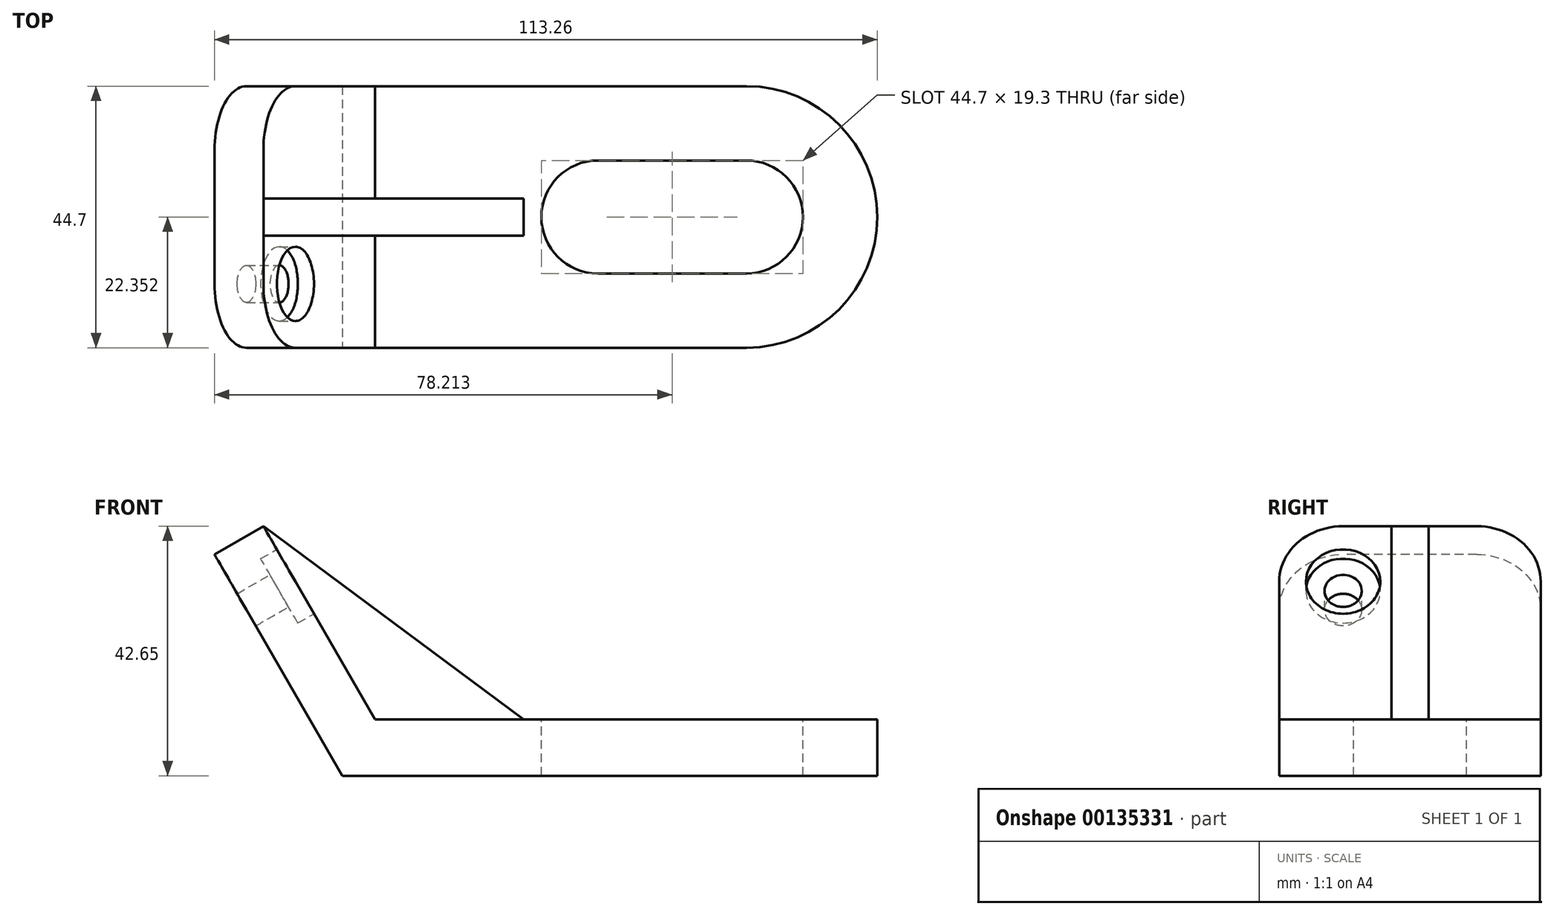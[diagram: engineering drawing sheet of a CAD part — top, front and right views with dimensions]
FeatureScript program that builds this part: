
annotation { "Feature Type Name" : "Feature", "Feature Type Description" : "" }
export const myFeature = defineFeature(function(context is Context, id is Id, definition is map)
    precondition{}
    {
        {
            var Q0;
            Q0=qCreatedBy(makeId("Front.planeOp"),FACE);
            var sketch = newSketch(context, id + "F0", { "sketchPlane" : qUnion([Q0])});
            skLineSegment(sketch, "E0", {"start": v(0, 0) * mm, "end": v(69.07, 0) * mm});
            skLineSegment(sketch, "E1", {"start": v(69.07, 0) * mm, "end": v(69.07, 9.65) * mm});
            skLineSegment(sketch, "E2", {"start": v(69.07, 9.65) * mm, "end": v(5.57, 9.65) * mm});
            skLineSegment(sketch, "E3", {"start": v(5.57, 9.65) * mm, "end": v(-13.48, 42.65) * mm});
            skLineSegment(sketch, "E4", {"start": v(-13.48, 42.65) * mm, "end": v(-21.84, 37.82) * mm});
            skLineSegment(sketch, "E5", {"start": v(-21.84, 37.82) * mm, "end": v(0, 0) * mm});
            skSolve(sketch);
        }
        {
            var Q0;
            Q0 = qSketchRegion(id + "F0", true);
            extrude(context, id + "F1", {"entities" : qUnion([Q0]), "oppositeDirection" : true, "depth" : 44.7 * mm});
        }
        {
            var Q0;
            Q0=makeQuery(id+"F1.opExtrude","SWEPT_FACE",FACE,{"disambiguationData":[OSD([sQuery(id+"F0.wireOp",EDGE,"E2")])]});
            var sketch = newSketch(context, id + "F2", { "sketchPlane" : qUnion([Q0])});
            skArc(sketch, "E6", {"start": v(69.07, 0) * mm, "mid": v(91.42, 22.35) * mm, "end": v(69.07, 44.7) * mm});
            skArc(sketch, "E7", {"start": v(69.07, 12.7) * mm, "mid": v(78.72, 22.35) * mm, "end": v(69.07, 32) * mm});
            skLineSegment(sketch, "E8", {"start": v(69.07, 22.35) * mm, "end": v(43.67, 22.35) * mm, "construction": true});
            skArc(sketch, "E9", {"start": v(43.67, 32) * mm, "mid": v(34.02, 22.35) * mm, "end": v(43.67, 12.7) * mm});
            skLineSegment(sketch, "E10", {"start": v(43.67, 32) * mm, "end": v(69.07, 32) * mm});
            skLineSegment(sketch, "E11", {"start": v(43.67, 12.7) * mm, "end": v(69.07, 12.7) * mm});
            skLineSegment(sketch, "E12.trimOffspring", {"start": v(69.07, 12.7) * mm, "end": v(69.07, 0) * mm});
            skLineSegment(sketch, "E13", {"start": v(5.57, 22.35) * mm, "end": v(30.97, 22.35) * mm, "construction": true});
            skPoint(sketch, "E13.endSnap0", {"position": v(34.02, 22.35) * mm});
            skSolve(sketch);
        }
        {
            var Q0;
            {var subQ0=sQuery(id+"F2.wireOp",EDGE,"E6");Q0=makeQuery(id+"F2.imprint","IMPRINT",FACE,{"disambiguationData":[TD([[makeQuery(id+"F2.imprint","IMPRINT",EDGE,{"derivedFrom":subQ0}),1.0]])]});}
            var Q1;
            Q1=makeQuery(id+"F1.opExtrude","SWEPT_FACE",FACE,{"disambiguationData":[OSD([sQuery(id+"F0.wireOp",EDGE,"E0")])]});
            extrude(context, id + "F3", {"entities" : qUnion([Q0]), "operationType" : NewBodyOperationType.ADD, "endBound" : BoundingType.UP_TO_SURFACE, "oppositeDirection" : true, "endBoundEntityFace" : qUnion([Q1]), "depth" : 25.4 * mm});
        }
        {
            var Q0;
            Q0=makeQuery(id+"F2.imprint","IMPRINT",FACE,{"disambiguationData":[TD([[makeQuery(id+"F2.imprint","IMPRINT",EDGE,{"derivedFrom":sQuery(id+"F2.wireOp",EDGE,"E9")}),1.0]])]});
            var Q1;
            {var subQ0=sQuery(id+"F0.wireOp",EDGE,"E0");Q1=makeQuery(id+"F3.boolean.opBoolean","MERGE",FACE,{"derivedFrom":[makeQuery(id+"F1.opExtrude","SWEPT_FACE",FACE,{"disambiguationData":[OSD([subQ0])]}),makeQuery(id+"F3.opExtrude","CAP_FACE",FACE,{"disambiguationData":[OSD([subQ0])],"isStart":false})]});}
            extrude(context, id + "F4", {"entities" : qUnion([Q0]), "operationType" : NewBodyOperationType.REMOVE, "endBound" : BoundingType.UP_TO_SURFACE, "oppositeDirection" : true, "endBoundEntityFace" : qUnion([Q1]), "depth" : 25.4 * mm});
        }
        {
            var Q0;
            Q0=qCreatedBy(makeId("Front.planeOp"),FACE);
            cPlane(context, id + "F5", {"entities" : qUnion([Q0]), "cplaneType" : CPlaneType.OFFSET, "offset" : 22.35 * mm, "oppositeDirection" : true, "width" : 152.4 * mm, "height" : 152.4 * mm});
        }
        {
            var Q0;
            Q0=makeQuery(id+"F1.opExtrude","SWEPT_FACE",FACE,{"disambiguationData":[OSD([sQuery(id+"F0.wireOp",EDGE,"E3")])]});
            var sketch = newSketch(context, id + "F6", { "sketchPlane" : qUnion([Q0])});
            skPoint(sketch, "E14", {"position": v(22.35, 43.67) * mm});
            skSolve(sketch);
        }
        {
            var Q0;
            Q0=qCreatedBy(id+"F5.planeOp",FACE);
            var sketch = newSketch(context, id + "F7", { "sketchPlane" : qUnion([Q0])});
            skPoint(sketch, "E15.0", {"position": v(30.97, 9.65) * mm});
            skPoint(sketch, "E16.0", {"position": v(-13.48, 42.65) * mm});
            skLineSegment(sketch, "E17", {"start": v(-13.48, 42.65) * mm, "end": v(30.97, 9.65) * mm});
            skPoint(sketch, "E18.0", {"position": v(5.57, 9.65) * mm});
            skLineSegment(sketch, "E19", {"start": v(30.97, 9.65) * mm, "end": v(5.57, 9.65) * mm});
            skLineSegment(sketch, "E20", {"start": v(-13.48, 42.65) * mm, "end": v(5.57, 9.65) * mm});
            skSolve(sketch);
        }
        {
            var Q0;
            Q0=makeQuery(id+"F7.imprint","IMPRINT",FACE,{"disambiguationData":[TD([[makeQuery(id+"F7.imprint","IMPRINT",EDGE,{"derivedFrom":sQuery(id+"F7.wireOp",EDGE,"E17")}),-1.0]])]});
            extrude(context, id + "F8", {"entities" : qUnion([Q0]), "operationType" : NewBodyOperationType.ADD, "endBound" : BoundingType.SYMMETRIC, "depth" : 6.35 * mm});
        }
        {
            var Q0;
            {var subQ0=sQuery(id+"F0.wireOp",EDGE,"E3");Q0=makeQuery(id+"F6.imprint","IMPRINT",FACE,{"disambiguationData":[TD([[makeQuery(id+"F6.imprint","IMPRINT",EDGE,{"derivedFrom":makeQuery(id+"F1.opExtrude","CAP_EDGE",EDGE,{"disambiguationData":[OSD([subQ0])],"isStart":true})}),-1.0]])]});}
            var sketch = newSketch(context, id + "F9", { "sketchPlane" : qUnion([Q0])});
            skLineSegment(sketch, "E21.0.0", {"start": v(0, 43.67) * mm, "end": v(0, 5.57) * mm});
            skLineSegment(sketch, "E21.0.1", {"start": v(0, 5.57) * mm, "end": v(44.7, 5.57) * mm});
            skLineSegment(sketch, "E21.0.2", {"start": v(44.7, 5.57) * mm, "end": v(44.7, 43.67) * mm});
            skLineSegment(sketch, "E21.0.3", {"start": v(44.7, 43.67) * mm, "end": v(0, 43.67) * mm});
            skLineSegment(sketch, "E22", {"start": v(44.7, 32.75) * mm, "end": v(33.78, 32.75) * mm});
            skLineSegment(sketch, "E23", {"start": v(44.7, 32.75) * mm, "end": v(10.92, 32.75) * mm});
            skPoint(sketch, "E24.0", {"position": v(22.35, 43.67) * mm});
            skCircle(sketch, "E25", {"center": v(33.78, 32.75) * mm, "radius": 6.35 * mm});
            skCircle(sketch, "E26", {"center": v(10.92, 32.75) * mm, "radius": 6.35 * mm});
            skCircle(sketch, "E27", {"center": v(10.92, 32.75) * mm, "radius": 3.18 * mm});
            skCircle(sketch, "E28", {"center": v(33.78, 32.75) * mm, "radius": 3.18 * mm});
            skSolve(sketch);
        }
        {
            var Q0;
            {var subQ0=sQuery(id+"F9.wireOp",EDGE,"E23");var subQ1=makeQuery(id+"F9.imprint","IMPRINT",VERTEX,{"derivedFrom":subQ0});Q0=makeQuery(id+"F9.imprint","IMPRINT",FACE,{"disambiguationData":[TD([[makeQuery(id+"F9.imprint","IMPRINT",EDGE,{"disambiguationData":[TD([[subQ1,1.0]])],"derivedFrom":subQ0}),-1.0]])]});}
            var Q1;
            {var subQ0=sQuery(id+"F9.wireOp",EDGE,"E23");var subQ1=makeQuery(id+"F9.imprint","IMPRINT",VERTEX,{"derivedFrom":subQ0});Q1=makeQuery(id+"F9.imprint","IMPRINT",FACE,{"disambiguationData":[TD([[makeQuery(id+"F9.imprint","IMPRINT",EDGE,{"disambiguationData":[TD([[subQ1,1.0]])],"derivedFrom":subQ0}),1.0]])]});}
            var Q2;
            Q2=makeQuery(id+"F9.imprint","IMPRINT",FACE,{"disambiguationData":[TD([[makeQuery(id+"F9.imprint","IMPRINT",EDGE,{"derivedFrom":sQuery(id+"F9.wireOp",EDGE,"E27")}),1.0]])]});
            var Q3;
            Q3=makeQuery(id+"F1.opExtrude","SWEPT_FACE",FACE,{"disambiguationData":[OSD([sQuery(id+"F0.wireOp",EDGE,"E5")])]});
            extrude(context, id + "F10", {"entities" : qUnion([Q0, Q1, Q2]), "operationType" : NewBodyOperationType.REMOVE, "endBound" : BoundingType.UP_TO_SURFACE, "oppositeDirection" : true, "endBoundEntityFace" : qUnion([Q3]), "depth" : 25.4 * mm});
        }
        {
            var Q0;
            Q0=makeQuery(id+"F9.imprint","IMPRINT",FACE,{"disambiguationData":[TD([[makeQuery(id+"F9.imprint","IMPRINT",EDGE,{"derivedFrom":sQuery(id+"F9.wireOp",EDGE,"E26")}),1.0]])]});
            var Q1;
            {var subQ0=sQuery(id+"F9.wireOp",EDGE,"E25");var subQ1=sQuery(id+"F9.wireOp",EDGE,"E23");var subQ2=makeQuery(id+"F9.imprint","INTERSECT",VERTEX,{"disambiguationData":[OD(0.0)],"derivedFrom":[subQ1,subQ0]});Q1=makeQuery(id+"F9.imprint","IMPRINT",FACE,{"disambiguationData":[TD([[makeQuery(id+"F9.imprint","IMPRINT",EDGE,{"disambiguationData":[TD([[subQ2,-1.0]])],"derivedFrom":subQ1}),1.0]])]});}
            var Q2;
            {var subQ0=sQuery(id+"F9.wireOp",EDGE,"E25");var subQ1=sQuery(id+"F9.wireOp",EDGE,"E23");var subQ2=makeQuery(id+"F9.imprint","INTERSECT",VERTEX,{"disambiguationData":[OD(0.0)],"derivedFrom":[subQ1,subQ0]});Q2=makeQuery(id+"F9.imprint","IMPRINT",FACE,{"disambiguationData":[TD([[makeQuery(id+"F9.imprint","IMPRINT",EDGE,{"disambiguationData":[TD([[subQ2,-1.0]])],"derivedFrom":subQ1}),-1.0]])]});}
            extrude(context, id + "F11", {"entities" : qUnion([Q0, Q1, Q2]), "operationType" : NewBodyOperationType.REMOVE, "oppositeDirection" : true, "depth" : 3.17 * mm});
        }
        {
            var Q0;
            Q0=makeQuery(id+"F1.opExtrude","CAP_EDGE",EDGE,{"disambiguationData":[OSD([sQuery(id+"F0.wireOp",EDGE,"E4")])],"isStart":true});
            var Q1;
            Q1=makeQuery(id+"F1.opExtrude","CAP_EDGE",EDGE,{"disambiguationData":[OSD([sQuery(id+"F0.wireOp",EDGE,"E4")])],"isStart":false});
            fillet(context, id + "F12", {"entities" : qUnion([Q0, Q1]), "radius" : 10.92 * mm, "tangentPropagation" : true, "allowEdgeOverflow" : false});
        }
    });
